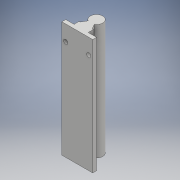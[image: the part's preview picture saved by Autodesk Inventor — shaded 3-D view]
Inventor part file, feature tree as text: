
AUTODESK INVENTOR PART (.ipt)
format: ipt  version: 2018 (Build 220112000, 112)  size: 127,488 bytes
history: native  units: mm
features: sketch x2, other x1, extrude x1, hole x1
ambient origin geometry x8: Origin, YZ Plane, XZ Plane, XY Plane, X Axis, Y Axis, Z Axis, Center Point
bodies: Body1 (feature_tree)
feature tree (5):
  other  "Sólido1"
  extrude  "Extrusão1"  Depth=25.0mm
  hole  "Furo1"  [1 undecoded]
  sketch  "Esboço1"  dims[d6=16.0mm d7=25.0mm]
  sketch  "Esboço3"  dims[d8=18.5mm d9=11.7mm d10=8.0mm d11=30.0deg d12=30.0deg d13=5.0mm d14=40.0mm d15=150.0mm d16=0.0mm d18=15.0mm d19=15.0mm d20=5.5mm d21=5.5mm d22=20.0mm d28=5.5mm d29=6.0mm d30=4.0mm d31=2.0mm d32=90.0deg d33=8.0mm d34=20.594885mm]
note: 1 required parameter value undecoded (feature->parameter linkage not recoverable at this tier; creation-order binding heuristic only, values carry confidence <= 0.55)
